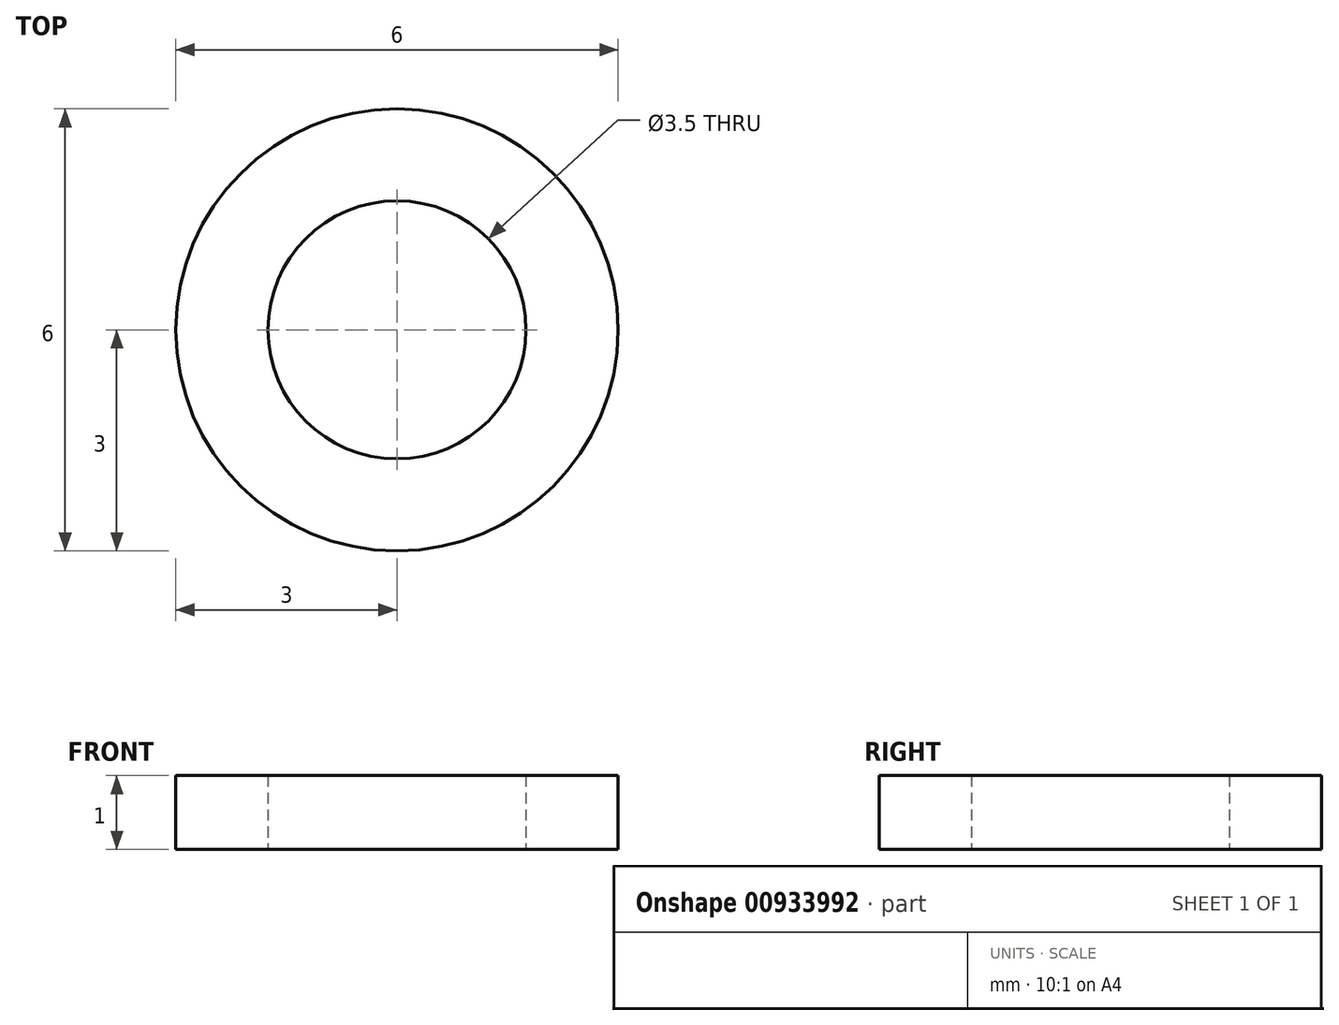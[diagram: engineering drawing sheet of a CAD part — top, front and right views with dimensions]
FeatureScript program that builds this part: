
annotation { "Feature Type Name" : "Feature", "Feature Type Description" : "" }
export const myFeature = defineFeature(function(context is Context, id is Id, definition is map)
    precondition{}
    {
        {
            var Q0;
            Q0=qCreatedBy(makeId("Top.planeOp"),FACE);
            var sketch = newSketch(context, id + "F0", { "sketchPlane" : qUnion([Q0])});
            skCircle(sketch, "E0", {"center": v(0, 0) * mm, "radius": 1.75 * mm});
            skCircle(sketch, "E1", {"center": v(0, 0) * mm, "radius": 3 * mm});
            skSolve(sketch);
        }
        {
            var Q0;
            Q0=makeQuery(id+"F0.imprint","IMPRINT",FACE,{"disambiguationData":[TD([[makeQuery(id+"F0.imprint","IMPRINT",EDGE,{"derivedFrom":sQuery(id+"F0.wireOp",EDGE,"E0")}),-1.0]])]});
            extrude(context, id + "F1", {"entities" : qUnion([Q0]), "depth" : 1 * mm, "offsetDistance" : 25 * mm});
        }
    });
